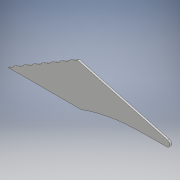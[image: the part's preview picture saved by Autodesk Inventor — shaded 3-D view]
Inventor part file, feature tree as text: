
AUTODESK INVENTOR PART (.ipt)
format: ipt  version: 2018.2 (Build 222227000, 227)  size: 105,984 bytes
history: native  units: mm
features: extrude x1, sketch x1
ambient origin geometry x8: Origin, YZ Plane, XZ Plane, XY Plane, X Axis, Y Axis, Z Axis, Center Point
bodies: Body1 (feature_tree)
feature tree (2):
  extrude  "押し出し2"  TaperAngle=15.0deg  [1 undecoded]
  sketch  "スケッチ1"
note: 1 required parameter value undecoded (feature->parameter linkage not recoverable at this tier; creation-order binding heuristic only, values carry confidence <= 0.55)
